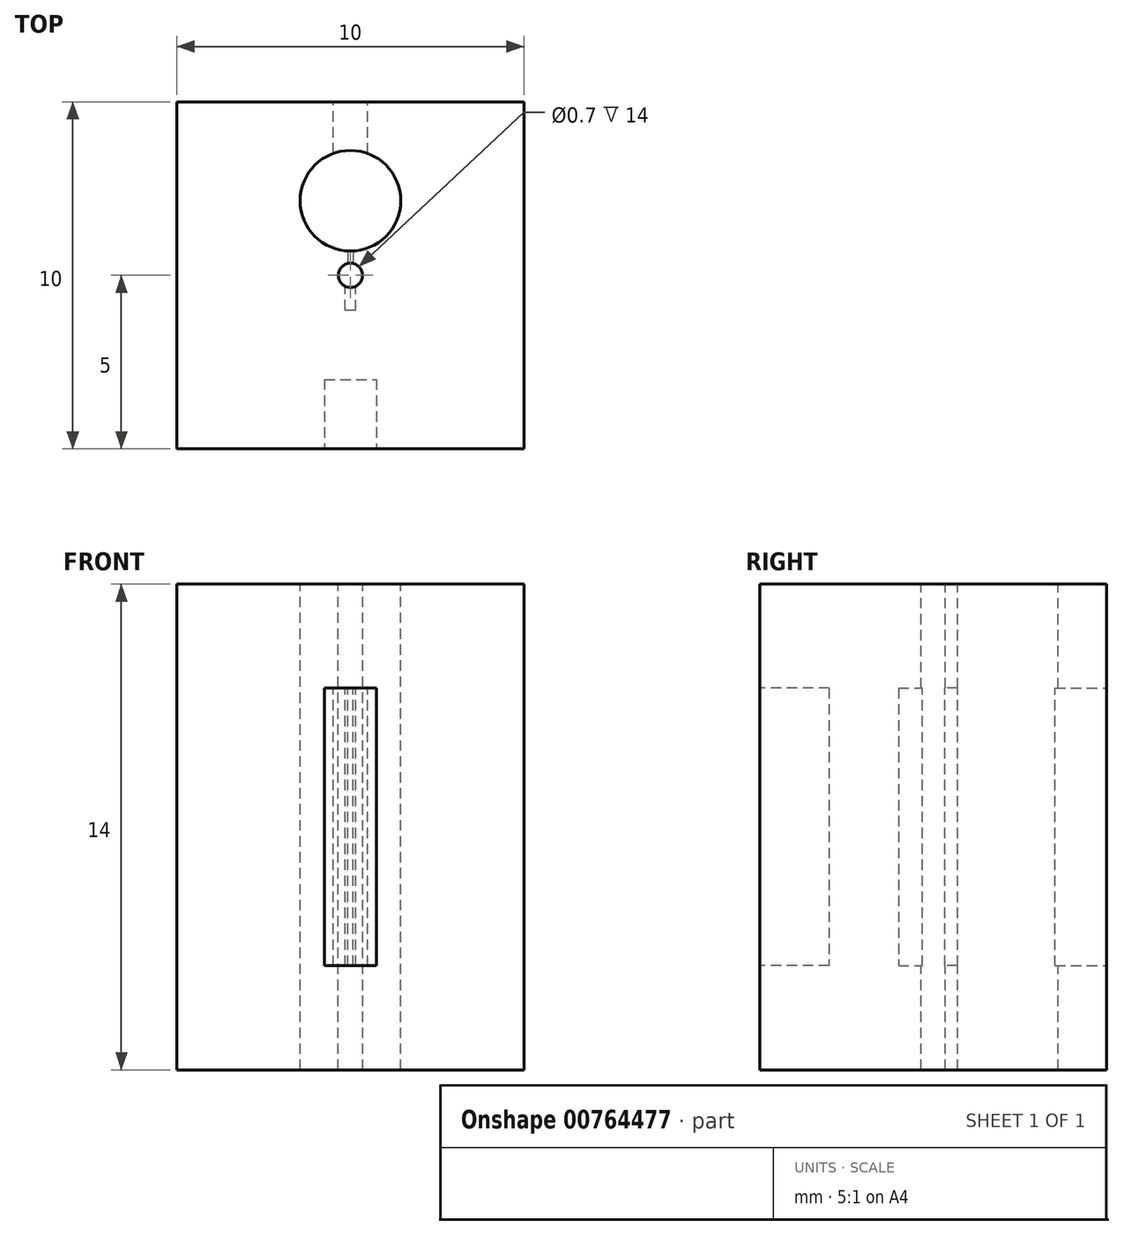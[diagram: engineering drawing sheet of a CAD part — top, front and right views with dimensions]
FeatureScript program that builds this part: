
annotation { "Feature Type Name" : "Feature", "Feature Type Description" : "" }
export const myFeature = defineFeature(function(context is Context, id is Id, definition is map)
    precondition{}
    {
        {
            var Q0;
            Q0=qCreatedBy(makeId("Top.planeOp"),FACE);
            var sketch = newSketch(context, id + "F0", { "sketchPlane" : qUnion([Q0])});
            skLineSegment(sketch, "E0.bottom", {"start": v(-5, 5) * mm, "end": v(5, 5) * mm});
            skLineSegment(sketch, "E0.top", {"start": v(-5, -5) * mm, "end": v(5, -5) * mm});
            skLineSegment(sketch, "E0.left", {"start": v(-5, 5) * mm, "end": v(-5, -5) * mm});
            skLineSegment(sketch, "E0.right", {"start": v(5, 5) * mm, "end": v(5, -5) * mm});
            skPoint(sketch, "E0.middle", {"position": v(0, 0) * mm});
            skSolve(sketch);
        }
        {
            var Q0;
            Q0=makeQuery(id+"F0.imprint","IMPRINT",FACE,{"disambiguationData":[TD([[makeQuery(id+"F0.imprint","IMPRINT",EDGE,{"derivedFrom":sQuery(id+"F0.wireOp",EDGE,"E0.bottom")}),-1.0]])]});
            extrude(context, id + "F1", {"entities" : qUnion([Q0]), "depth" : 14 * mm, "offsetDistance" : 25 * mm});
        }
        {
            var Q0;
            Q0=makeQuery(id+"F1.opExtrude","CAP_FACE",FACE,{"disambiguationData":[OSD([sQuery(id+"F0.wireOp",EDGE,"E0.bottom"),sQuery(id+"F0.wireOp",EDGE,"E0.top"),sQuery(id+"F0.wireOp",EDGE,"E0.left"),sQuery(id+"F0.wireOp",EDGE,"E0.right")])],"isStart":false});
            var sketch = newSketch(context, id + "F2", { "sketchPlane" : qUnion([Q0])});
            skCircle(sketch, "E1", {"center": v(0, 0) * mm, "radius": 0.35 * mm});
            skSolve(sketch);
        }
        {
            var Q0;
            Q0 = qSketchRegion(id + "F2", true);
            extrude(context, id + "F3", {"entities" : qUnion([Q0]), "operationType" : NewBodyOperationType.REMOVE, "oppositeDirection" : true, "depth" : 14 * mm, "offsetDistance" : 25 * mm});
        }
        {
            var Q0;
            Q0=makeQuery(id+"F1.opExtrude","CAP_FACE",FACE,{"disambiguationData":[OSD([sQuery(id+"F0.wireOp",EDGE,"E0.bottom"),sQuery(id+"F0.wireOp",EDGE,"E0.top"),sQuery(id+"F0.wireOp",EDGE,"E0.left"),sQuery(id+"F0.wireOp",EDGE,"E0.right")])],"isStart":false});
            var sketch = newSketch(context, id + "F4", { "sketchPlane" : qUnion([Q0])});
            skCircle(sketch, "E2", {"center": v(0, 2.15) * mm, "radius": 1.45 * mm});
            skSolve(sketch);
        }
        {
            var Q0;
            Q0 = qSketchRegion(id + "F4", true);
            extrude(context, id + "F5", {"entities" : qUnion([Q0]), "operationType" : NewBodyOperationType.REMOVE, "oppositeDirection" : true, "depth" : 14 * mm, "offsetDistance" : 25 * mm});
        }
        {
            var Q0;
            Q0=makeQuery(id+"F1.opExtrude","SWEPT_FACE",FACE,{"disambiguationData":[OSD([sQuery(id+"F0.wireOp",EDGE,"E0.bottom")])]});
            var sketch = newSketch(context, id + "F6", { "sketchPlane" : qUnion([Q0])});
            skLineSegment(sketch, "E3.bottom", {"start": v(0.5, 3) * mm, "end": v(-0.5, 3) * mm});
            skLineSegment(sketch, "E3.top", {"start": v(0.5, 11) * mm, "end": v(-0.5, 11) * mm});
            skLineSegment(sketch, "E3.left", {"start": v(0.5, 3) * mm, "end": v(0.5, 11) * mm});
            skLineSegment(sketch, "E3.right", {"start": v(-0.5, 3) * mm, "end": v(-0.5, 11) * mm});
            skPoint(sketch, "E3.middle", {"position": v(0, 7) * mm});
            skSolve(sketch);
        }
        {
            var Q0;
            Q0 = qSketchRegion(id + "F6", true);
            extrude(context, id + "F7", {"entities" : qUnion([Q0]), "operationType" : NewBodyOperationType.REMOVE, "oppositeDirection" : true, "depth" : 2 * mm, "offsetDistance" : 25 * mm});
        }
        {
            var Q0;
            Q0=qCreatedBy(makeId("Front.planeOp"),FACE);
            var sketch = newSketch(context, id + "F8", { "sketchPlane" : qUnion([Q0])});
            skLineSegment(sketch, "E4.bottom", {"start": v(-0.08, 3) * mm, "end": v(0.07, 3) * mm});
            skLineSegment(sketch, "E4.top", {"start": v(-0.08, 11) * mm, "end": v(0.07, 11) * mm});
            skLineSegment(sketch, "E4.left", {"start": v(-0.08, 3) * mm, "end": v(-0.08, 11) * mm});
            skLineSegment(sketch, "E4.right", {"start": v(0.07, 3) * mm, "end": v(0.07, 11) * mm});
            skPoint(sketch, "E4.middle", {"position": v(0, 7) * mm});
            skSolve(sketch);
        }
        {
            var Q0;
            Q0 = qSketchRegion(id + "F8", true);
            extrude(context, id + "F9", {"entities" : qUnion([Q0]), "operationType" : NewBodyOperationType.REMOVE, "oppositeDirection" : true, "depth" : 1 * mm, "offsetDistance" : 25 * mm});
        }
        {
            var Q0;
            Q0=qCreatedBy(makeId("Front.planeOp"),FACE);
            var sketch = newSketch(context, id + "F10", { "sketchPlane" : qUnion([Q0])});
            skLineSegment(sketch, "E5.bottom", {"start": v(-0.15, 11) * mm, "end": v(0.15, 11) * mm});
            skLineSegment(sketch, "E5.top", {"start": v(-0.15, 3) * mm, "end": v(0.15, 3) * mm});
            skLineSegment(sketch, "E5.left", {"start": v(-0.15, 11) * mm, "end": v(-0.15, 3) * mm});
            skLineSegment(sketch, "E5.right", {"start": v(0.15, 11) * mm, "end": v(0.15, 3) * mm});
            skPoint(sketch, "E5.middle", {"position": v(0, 7) * mm});
            skSolve(sketch);
        }
        {
            var Q0;
            Q0 = qSketchRegion(id + "F10", true);
            extrude(context, id + "F11", {"entities" : qUnion([Q0]), "operationType" : NewBodyOperationType.REMOVE, "depth" : 1 * mm, "offsetDistance" : 25 * mm});
        }
        {
            var Q0;
            Q0=makeQuery(id+"F1.opExtrude","SWEPT_FACE",FACE,{"disambiguationData":[OSD([sQuery(id+"F0.wireOp",EDGE,"E0.top")])]});
            var sketch = newSketch(context, id + "F12", { "sketchPlane" : qUnion([Q0])});
            skLineSegment(sketch, "E6.bottom", {"start": v(-0.75, 11) * mm, "end": v(0.75, 11) * mm});
            skLineSegment(sketch, "E6.top", {"start": v(-0.75, 3) * mm, "end": v(0.75, 3) * mm});
            skLineSegment(sketch, "E6.left", {"start": v(-0.75, 11) * mm, "end": v(-0.75, 3) * mm});
            skLineSegment(sketch, "E6.right", {"start": v(0.75, 11) * mm, "end": v(0.75, 3) * mm});
            skPoint(sketch, "E6.middle", {"position": v(0, 7) * mm});
            skSolve(sketch);
        }
        {
            var Q0;
            Q0 = qSketchRegion(id + "F12", true);
            extrude(context, id + "F13", {"entities" : qUnion([Q0]), "operationType" : NewBodyOperationType.REMOVE, "oppositeDirection" : true, "depth" : 2 * mm, "offsetDistance" : 25 * mm});
        }
    });
